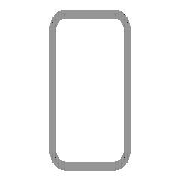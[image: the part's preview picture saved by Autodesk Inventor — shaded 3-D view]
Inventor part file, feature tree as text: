
AUTODESK INVENTOR PART (.ipt)
format: ipt  version: 2025.3 (Build 293356000, 356)  size: 150,016 bytes
history: native  units: mm (DEFAULTED — no unit token found)
features: other x4, plane x3, split x2, sketch x1
ambient origin geometry x8: Origin, YZ Plane, XZ Plane, XY Plane, X Axis, Y Axis, Z Axis, Center Point
bodies: Solid1 (feature_tree), Body (feature_tree)
feature tree (10):
  parser-record x1  (decoder bookkeeping rows leaked as tree rows — omitted from the tree; the rows remain in map.json)
  other  "Driven Length"
  other  "Start Plane"
  other  "End Plane"
  plane  "Work Plane4"
  split  "Split1"
  plane  "Work Plane5"
  split  "Split2"
  sketch  "Sketch3"  dims[d3=2701.920698mm d4=0.0mm d7=4.0mm d9=20.0mm d11=40.0mm d12=2.0mm d13=77.445959mm d14=2779.366657mm d15=10.0mm d16=20.0mm d17=90.0deg d18=2701.920698mm]
  plane  "Work Plane3"
